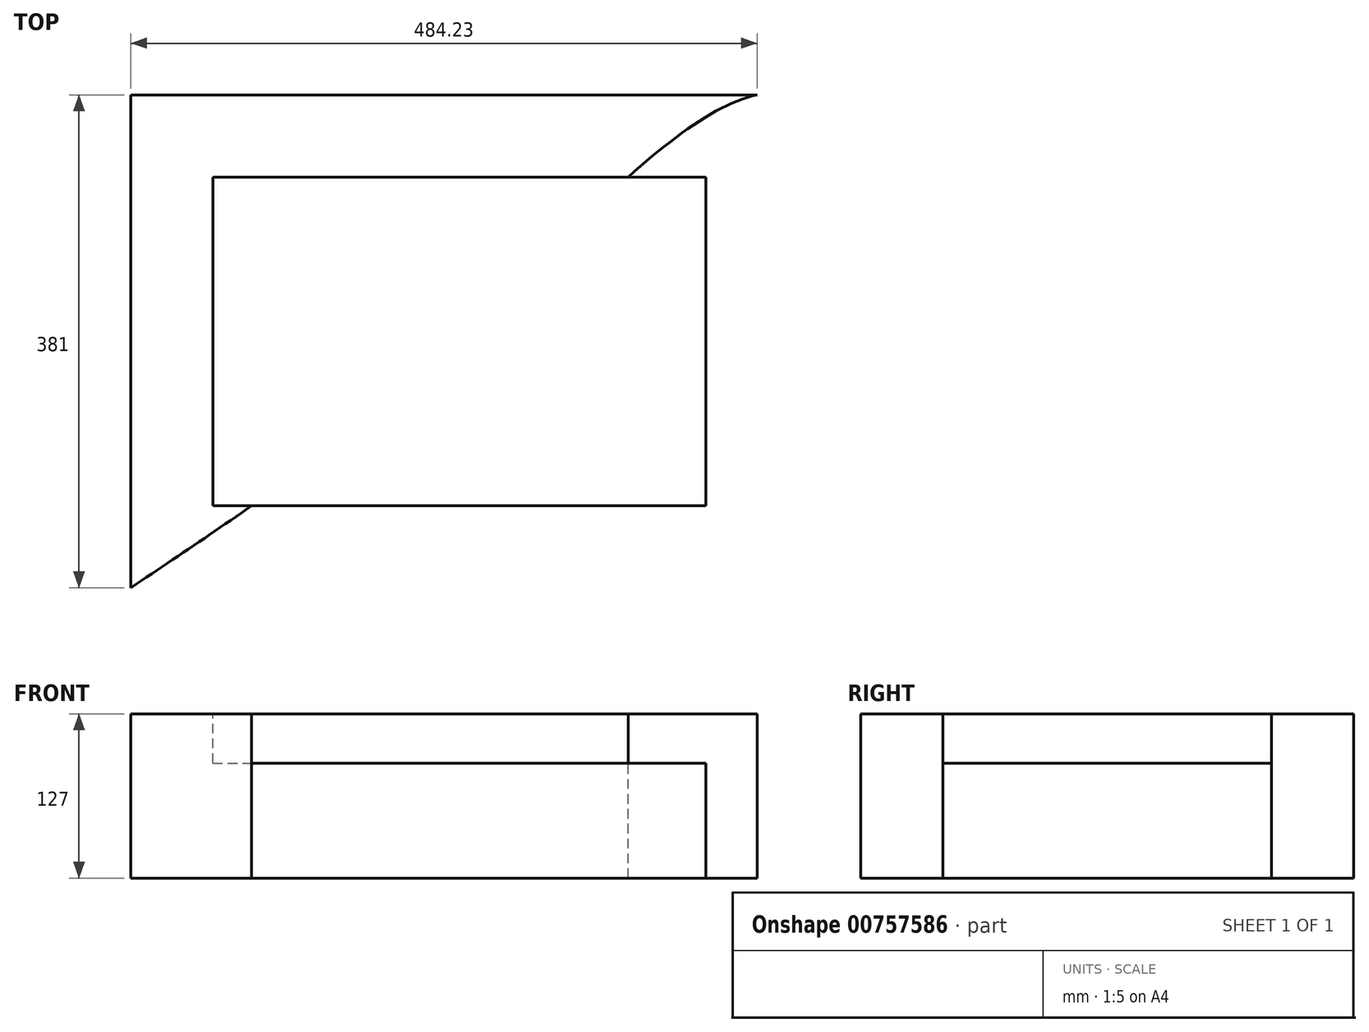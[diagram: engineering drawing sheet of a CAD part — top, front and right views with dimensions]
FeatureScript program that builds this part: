
annotation { "Feature Type Name" : "Feature", "Feature Type Description" : "" }
export const myFeature = defineFeature(function(context is Context, id is Id, definition is map)
    precondition{}
    {
        {
            var Q0;
            Q0=qCreatedBy(makeId("Top.planeOp"),FACE);
            var sketch = newSketch(context, id + "F0", { "sketchPlane" : qUnion([Q0])});
            skLineSegment(sketch, "E0", {"start": v(0, 0) * mm, "end": v(508, 0) * mm});
            skLineSegment(sketch, "E1", {"start": v(0, 0) * mm, "end": v(0, 381) * mm});
            skLineSegment(sketch, "E2", {"start": v(508, 0) * mm, "end": v(508, 381) * mm});
            skLineSegment(sketch, "E3", {"start": v(508, 381) * mm, "end": v(0, 381) * mm});
            skSolve(sketch);
        }
        {
            var Q0;
            Q0=makeQuery(id+"F0.imprint","IMPRINT",FACE,{"disambiguationData":[TD([[makeQuery(id+"F0.imprint","IMPRINT",EDGE,{"derivedFrom":sQuery(id+"F0.wireOp",EDGE,"E0")}),1.0]])]});
            extrude(context, id + "F1", {"entities" : qUnion([Q0]), "depth" : 127 * mm, "offsetDistance" : 25.4 * mm});
        }
        {
            var Q0;
            Q0=makeQuery(id+"F1.opExtrude","CAP_FACE",FACE,{"disambiguationData":[OSD([sQuery(id+"F0.wireOp",EDGE,"E0"),sQuery(id+"F0.wireOp",EDGE,"E1"),sQuery(id+"F0.wireOp",EDGE,"E2"),sQuery(id+"F0.wireOp",EDGE,"E3")])],"isStart":false});
            var sketch = newSketch(context, id + "F2", { "sketchPlane" : qUnion([Q0])});
            skLineSegment(sketch, "E4.bottom", {"start": v(63.5, 317.5) * mm, "end": v(444.5, 317.5) * mm});
            skLineSegment(sketch, "E4.top", {"start": v(63.5, 63.5) * mm, "end": v(444.5, 63.5) * mm});
            skLineSegment(sketch, "E4.left", {"start": v(63.5, 317.5) * mm, "end": v(63.5, 63.5) * mm});
            skLineSegment(sketch, "E4.right", {"start": v(444.5, 317.5) * mm, "end": v(444.5, 63.5) * mm});
            skLineSegment(sketch, "E5.0.0", {"start": v(508, 0) * mm, "end": v(508, 381) * mm});
            skLineSegment(sketch, "E5.0.1", {"start": v(508, 381) * mm, "end": v(0, 381) * mm});
            skLineSegment(sketch, "E5.0.2", {"start": v(0, 381) * mm, "end": v(0, 0) * mm});
            skLineSegment(sketch, "E5.0.3", {"start": v(0, 0) * mm, "end": v(508, 0) * mm});
            skSolve(sketch);
        }
        {
            var Q0;
            Q0=makeQuery(id+"F2.imprint","IMPRINT",FACE,{"disambiguationData":[TD([[makeQuery(id+"F2.imprint","IMPRINT",EDGE,{"derivedFrom":sQuery(id+"F2.wireOp",EDGE,"E4.bottom")}),-1.0]])]});
            extrude(context, id + "F3", {"entities" : qUnion([Q0]), "operationType" : NewBodyOperationType.REMOVE, "oppositeDirection" : true, "depth" : 38.1 * mm, "offsetDistance" : 25.4 * mm});
        }
        {
            var Q0;
            Q0=makeQuery(id+"F1.opExtrude","CAP_FACE",FACE,{"disambiguationData":[OSD([sQuery(id+"F0.wireOp",EDGE,"E0"),sQuery(id+"F0.wireOp",EDGE,"E1"),sQuery(id+"F0.wireOp",EDGE,"E2"),sQuery(id+"F0.wireOp",EDGE,"E3")])],"isStart":false});
            var sketch = newSketch(context, id + "F4", { "sketchPlane" : qUnion([Q0])});
            skFitSpline(sketch, "E6", {"points": [v(0, 0) * mm, v(260.52, 198.64) * mm, v(508, 381) * mm, v(616.51, 0) * mm], "startDerivative": vector(773.16, 514.54) * mm, "endDerivative": vector(168.13, -1523.7) * mm});
            skLineSegment(sketch, "E7", {"start": v(0, 0) * mm, "end": v(616.51, 0) * mm});
            skSolve(sketch);
        }
        {
            var Q0;
            {var subQ5=makeQuery(id+"F3.boolean.opBoolean","COPY",EDGE,{"derivedFrom":makeQuery(id+"F3.opExtrude","CAP_EDGE",EDGE,{"disambiguationData":[OSD([sQuery(id+"F2.wireOp",EDGE,"E4.right")])],"isStart":true})});Q0=makeQuery(id+"F4.imprint","IMPRINT",FACE,{"disambiguationData":[TD([[makeQuery(id+"F4.imprint","IMPRINT",EDGE,{"derivedFrom":subQ5}),-1.0]])]});}
            var Q1;
            {var subQ0=makeQuery(id+"F1.opExtrude","CAP_EDGE",EDGE,{"disambiguationData":[OSD([sQuery(id+"F0.wireOp",EDGE,"E2")])],"isStart":false});Q1=makeQuery(id+"F4.imprint","IMPRINT",FACE,{"disambiguationData":[TD([[makeQuery(id+"F4.imprint","IMPRINT",EDGE,{"derivedFrom":subQ0}),1.0]])]});}
            var Q2;
            {var subQ1=makeQuery(id+"F1.opExtrude","CAP_EDGE",EDGE,{"disambiguationData":[OSD([sQuery(id+"F0.wireOp",EDGE,"E2")])],"isStart":false});Q2=makeQuery(id+"F4.imprint","IMPRINT",FACE,{"disambiguationData":[TD([[makeQuery(id+"F4.imprint","IMPRINT",EDGE,{"derivedFrom":subQ1}),-1.0]])]});}
            extrude(context, id + "F5", {"entities" : qUnion([Q0, Q1, Q2]), "operationType" : NewBodyOperationType.REMOVE, "endBound" : BoundingType.THROUGH_ALL, "oppositeDirection" : true, "depth" : 25.4 * mm, "offsetDistance" : 25.4 * mm});
        }
    });
